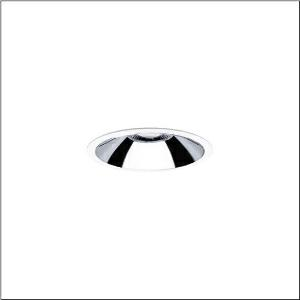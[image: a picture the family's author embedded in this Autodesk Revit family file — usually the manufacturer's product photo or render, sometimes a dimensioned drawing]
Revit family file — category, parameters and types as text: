
# Revit family: lunis_21_l_51db15md3c
name_source: partatom
category: Lighting Fixtures
units: mm (PartAtom-declared; Revit-internal decimal feet)

## family parameters
Cut with Voids When Loaded = No
Host = Face
Light Source = No
Part Type = Normal
Room Calculation Point = No
Round Connector Dimension = Use Diameter
Shared = No

## types (1)
- --- (1 x LED, 1670 lm, 13.8 W, 3000K)
    Apparent Load = 14 VA
    CIE Flux Codes = 90 99 100 100 100
    Color Rendering = 80
    Color Temperature = 3000K
    Default Elevation = 1800 mm
    Description = Lunis 21,  L, downlight, of PC, light emission: direct distribution, LED rated luminous flux: 1.670lm, light colour: 830, control gear: ECG, with terminal, 3-pole, mains connection: 220..240V, AC, housing, round, of diecast aluminium, traffic white (RAL 9016), diameter: 162mm, protection rating (complete): IP20, protection rating (on room side): IP54, insulation class (complete): insulation class II (safety insulation), certification: CE, impact resistance: IK02, packaging unit: 1 piece
    Height = 0 mm  [stored 0 ft]
    Lamp = 1 x LED
    Lamp Light Flux = 1670 lm
    Lamp Power = 13.8 W
    Lamp count = 1
    Length = 162 mm
    Luminous efficacy = 121 lm/W
    Manufacturer = Siteco
    ModVariant = No
    Model = 51DB15MD3C
    Mounting Place = Ceiling
    Mounting Type = Recessed
    Number of Poles = 1
    OnlyDefault = Yes
    Power Factor = 1
    Product Name = Lunis 21 L
    Product group = downlight
    ProductGroupID = 400
    Protection Class = Protection class II
    Protection Degree = IP 20
    RLX_Detail_Level = 1
    RLX_Emergency_Light_Flux = 0 lm
    RLX_Emergency_Type = 0
    RLX_Emergency_Type_DB = No
    RlxData = <blob elided: 21821 chars, md5=11f8cd3a>
    Socket = socket
    Standby Power = 0 W
    System Light Flux = 1670 lm
    System Power = 14 W
    Type Comments = factory setting: luminous flux: 100 % | (ON | ON)
    Type Image = l_1287387.jpg
    URL = http://relux.com
    VarID = @adj_117413
    Voltage = 0 V
    Weight = 0.00 kg
    Width = 0 mm  [stored 0 ft]

note: [stored X ft] marks values corroborated as IEEE doubles in the binary element streams (Revit-internal decimal feet)

## geometry (parser evidence)
native form markers: Blend x4, Sweep x9
no freeform markers — native parametric forms only
